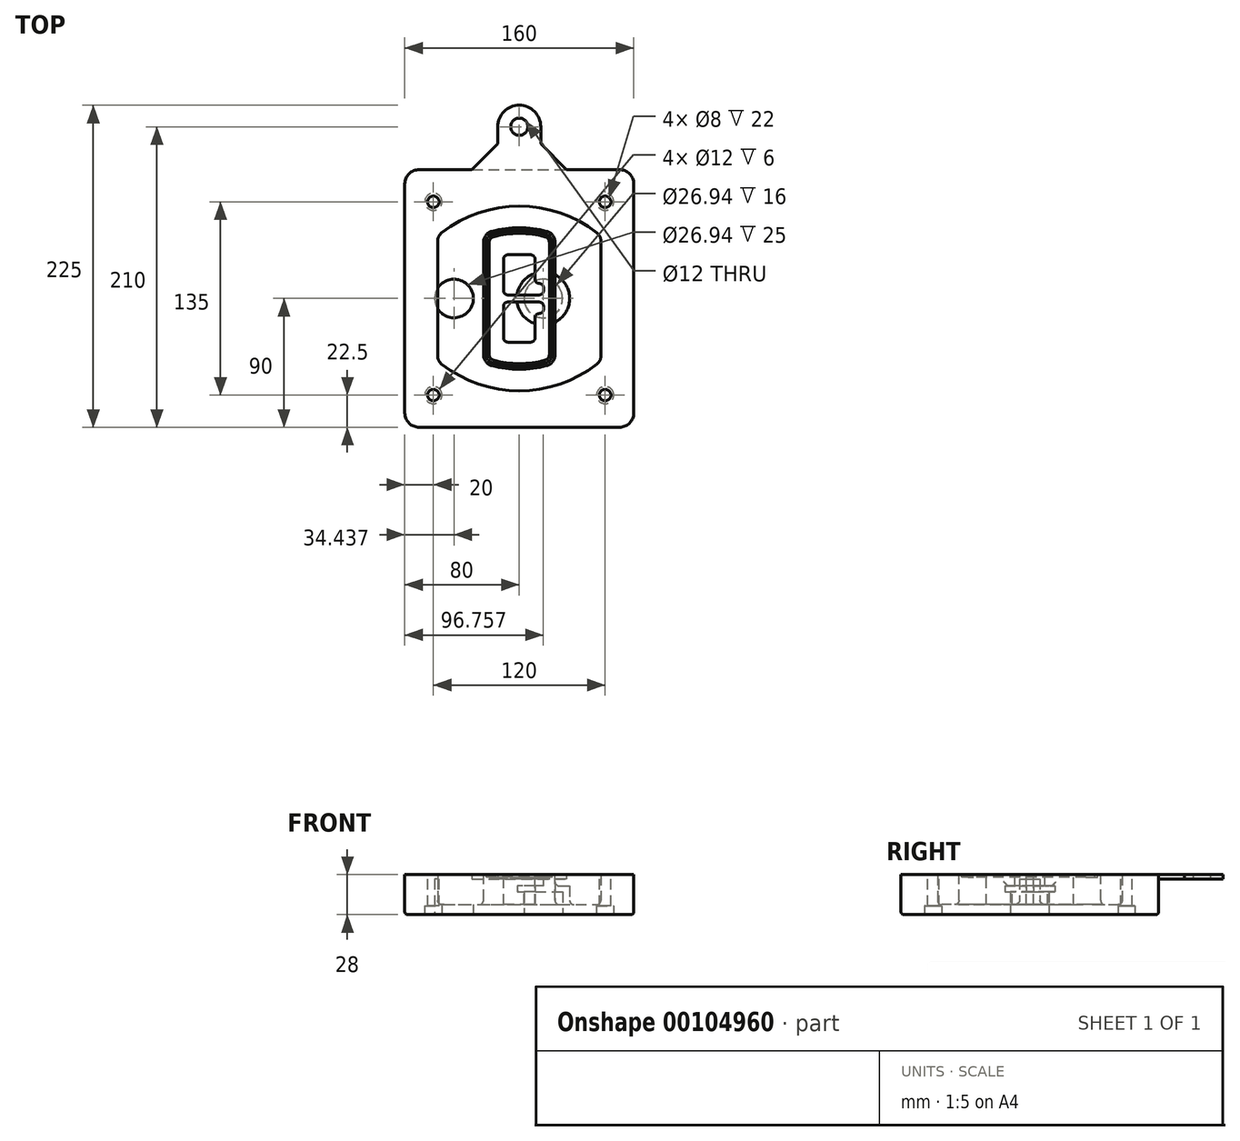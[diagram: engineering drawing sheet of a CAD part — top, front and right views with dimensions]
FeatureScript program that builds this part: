
annotation { "Feature Type Name" : "Feature", "Feature Type Description" : "" }
export const myFeature = defineFeature(function(context is Context, id is Id, definition is map)
    precondition{}
    {
        {
            var Q0;
            Q0=qCreatedBy(makeId("Top.planeOp"),FACE);
            var sketch = newSketch(context, id + "F0", { "sketchPlane" : qUnion([Q0])});
            skPoint(sketch, "E0.rect.middle", {"position": v(0, 0) * mm});
            skLineSegment(sketch, "E1.bottom", {"start": v(-70, -90) * mm, "end": v(70, -90) * mm});
            skLineSegment(sketch, "E1.top", {"start": v(-70, 90) * mm, "end": v(70, 90) * mm});
            skLineSegment(sketch, "E1.left", {"start": v(-80, -80) * mm, "end": v(-80, 80) * mm});
            skLineSegment(sketch, "E1.right", {"start": v(80, -80) * mm, "end": v(80, 80) * mm});
            skLineSegment(sketch, "E2", {"start": v(-80, 90) * mm, "end": v(80, -90) * mm, "construction": true});
            skLineSegment(sketch, "E3", {"start": v(80, 90) * mm, "end": v(-80, -90) * mm, "construction": true});
            skCircle(sketch, "E4", {"center": v(-60, 67.5) * mm, "radius": 4 * mm});
            skCircle(sketch, "E5", {"center": v(60, 67.5) * mm, "radius": 4 * mm});
            skCircle(sketch, "E6", {"center": v(60, -67.5) * mm, "radius": 4 * mm});
            skCircle(sketch, "E7", {"center": v(-60, -67.5) * mm, "radius": 4 * mm});
            skLineSegment(sketch, "E8", {"start": v(-60, 67.5) * mm, "end": v(60, 67.5) * mm, "construction": true});
            skLineSegment(sketch, "E9", {"start": v(60, 67.5) * mm, "end": v(60, -67.5) * mm, "construction": true});
            skLineSegment(sketch, "E10", {"start": v(60, -67.5) * mm, "end": v(-60, -67.5) * mm, "construction": true});
            skLineSegment(sketch, "E11", {"start": v(-60, -67.5) * mm, "end": v(-60, 67.5) * mm, "construction": true});
            skLineSegment(sketch, "E12", {"start": v(-60, 40.3) * mm, "end": v(-60, -40.3) * mm});
            skLineSegment(sketch, "E13", {"start": v(60, 40.3) * mm, "end": v(60, -40.3) * mm});
            skArc(sketch, "E14", {"start": v(56.15, 48.18) * mm, "mid": v(0, 67.5) * mm, "end": v(-56.15, 48.18) * mm});
            skArc(sketch, "E15", {"start": v(-56.15, -48.18) * mm, "mid": v(0, -67.5) * mm, "end": v(56.15, -48.18) * mm});
            skLineSegment(sketch, "E16", {"start": v(-60, 0) * mm, "end": v(60, 0) * mm, "construction": true});
            skPoint(sketch, "E17.visualSharp", {"position": v(-60, -45) * mm});
            skArc(sketch, "E17.filletArc", {"start": v(-60, -40.3) * mm, "mid": v(-58.99, -44.68) * mm, "end": v(-56.15, -48.18) * mm});
            skPoint(sketch, "E18.visualSharp", {"position": v(-60, 45) * mm});
            skArc(sketch, "E18.filletArc", {"start": v(-56.15, 48.18) * mm, "mid": v(-58.99, 44.68) * mm, "end": v(-60, 40.3) * mm});
            skPoint(sketch, "E19.visualSharp", {"position": v(60, 45) * mm});
            skArc(sketch, "E19.filletArc", {"start": v(60, 40.3) * mm, "mid": v(58.99, 44.68) * mm, "end": v(56.15, 48.18) * mm});
            skPoint(sketch, "E20.visualSharp", {"position": v(60, -45) * mm});
            skArc(sketch, "E20.filletArc", {"start": v(56.15, -48.18) * mm, "mid": v(58.99, -44.68) * mm, "end": v(60, -40.3) * mm});
            skPoint(sketch, "E21.visualSharp", {"position": v(-80, 90) * mm});
            skArc(sketch, "E21.filletArc", {"start": v(-70, 90) * mm, "mid": v(-77.07, 87.07) * mm, "end": v(-80, 80) * mm});
            skPoint(sketch, "E22.visualSharp", {"position": v(80, 90) * mm});
            skArc(sketch, "E22.filletArc", {"start": v(80, 80) * mm, "mid": v(77.07, 87.07) * mm, "end": v(70, 90) * mm});
            skPoint(sketch, "E23.visualSharp", {"position": v(80, -90) * mm});
            skArc(sketch, "E23.filletArc", {"start": v(70, -90) * mm, "mid": v(77.07, -87.07) * mm, "end": v(80, -80) * mm});
            skPoint(sketch, "E24.visualSharp", {"position": v(-80, -90) * mm});
            skArc(sketch, "E24.filletArc", {"start": v(-80, -80) * mm, "mid": v(-77.07, -87.07) * mm, "end": v(-70, -90) * mm});
            skArc(sketch, "E25.0", {"start": v(57, 40.3) * mm, "mid": v(56.3, 43.36) * mm, "end": v(54.3, 45.81) * mm});
            skLineSegment(sketch, "E25.1", {"start": v(57, 40.3) * mm, "end": v(57, -40.3) * mm});
            skArc(sketch, "E25.2", {"start": v(54.3, -45.81) * mm, "mid": v(56.3, -43.36) * mm, "end": v(57, -40.3) * mm});
            skArc(sketch, "E25.3", {"start": v(-54.3, -45.81) * mm, "mid": v(0, -64.5) * mm, "end": v(54.3, -45.81) * mm});
            skArc(sketch, "E25.4", {"start": v(-57, -40.3) * mm, "mid": v(-56.3, -43.36) * mm, "end": v(-54.3, -45.81) * mm});
            skArc(sketch, "E25.5", {"start": v(54.3, 45.81) * mm, "mid": v(0, 64.5) * mm, "end": v(-54.3, 45.81) * mm});
            skLineSegment(sketch, "E25.6", {"start": v(-57, 40.3) * mm, "end": v(-57, -40.3) * mm});
            skArc(sketch, "E25.7", {"start": v(-54.3, 45.81) * mm, "mid": v(-56.3, 43.36) * mm, "end": v(-57, 40.3) * mm});
            skArc(sketch, "E26.0", {"start": v(-58.62, 51.33) * mm, "mid": v(-62.58, 46.43) * mm, "end": v(-64, 40.3) * mm});
            skArc(sketch, "E26.1", {"start": v(58.62, 51.33) * mm, "mid": v(0, 71.5) * mm, "end": v(-58.62, 51.33) * mm});
            skArc(sketch, "E26.2", {"start": v(64, 40.3) * mm, "mid": v(62.58, 46.43) * mm, "end": v(58.62, 51.33) * mm});
            skLineSegment(sketch, "E26.3", {"start": v(64, 40.3) * mm, "end": v(64, -40.3) * mm});
            skArc(sketch, "E26.4", {"start": v(58.62, -51.33) * mm, "mid": v(62.58, -46.43) * mm, "end": v(64, -40.3) * mm});
            skLineSegment(sketch, "E26.5", {"start": v(-64, 40.3) * mm, "end": v(-64, -40.3) * mm});
            skArc(sketch, "E26.6", {"start": v(-58.62, -51.33) * mm, "mid": v(0, -71.5) * mm, "end": v(58.62, -51.33) * mm});
            skArc(sketch, "E26.7", {"start": v(-64, -40.3) * mm, "mid": v(-62.58, -46.43) * mm, "end": v(-58.62, -51.33) * mm});
            skSolve(sketch);
        }
        {
            var Q0;
            Q0=makeQuery(id+"F0.imprint","IMPRINT",FACE,{"disambiguationData":[TD([[makeQuery(id+"F0.imprint","IMPRINT",EDGE,{"derivedFrom":sQuery(id+"F0.wireOp",EDGE,"E1.bottom")}),1.0]])]});
            var Q1;
            Q1=makeQuery(id+"F0.imprint","IMPRINT",FACE,{"disambiguationData":[TD([[makeQuery(id+"F0.imprint","IMPRINT",EDGE,{"derivedFrom":sQuery(id+"F0.wireOp",EDGE,"E12")}),1.0]])]});
            var Q2;
            Q2=makeQuery(id+"F0.imprint","IMPRINT",FACE,{"disambiguationData":[TD([[makeQuery(id+"F0.imprint","IMPRINT",EDGE,{"derivedFrom":sQuery(id+"F0.wireOp",EDGE,"E25.0")}),1.0]])]});
            var Q3;
            Q3=makeQuery(id+"F0.imprint","IMPRINT",FACE,{"disambiguationData":[TD([[makeQuery(id+"F0.imprint","IMPRINT",EDGE,{"derivedFrom":sQuery(id+"F0.wireOp",EDGE,"E12")}),-1.0]])]});
            extrude(context, id + "F1", {"entities" : qUnion([Q0, Q1, Q2, Q3]), "oppositeDirection" : true, "depth" : 25 * mm});
        }
        {
            var Q0;
            Q0=makeQuery(id+"F0.imprint","IMPRINT",FACE,{"disambiguationData":[TD([[makeQuery(id+"F0.imprint","IMPRINT",EDGE,{"derivedFrom":sQuery(id+"F0.wireOp",EDGE,"E12")}),1.0]])]});
            extrude(context, id + "F2", {"entities" : qUnion([Q0]), "operationType" : NewBodyOperationType.ADD, "depth" : 3 * mm});
        }
        {
            var Q0;
            Q0=makeQuery(id+"F0.imprint","IMPRINT",FACE,{"disambiguationData":[TD([[makeQuery(id+"F0.imprint","IMPRINT",EDGE,{"derivedFrom":sQuery(id+"F0.wireOp",EDGE,"E25.0")}),1.0]])]});
            extrude(context, id + "F3", {"entities" : qUnion([Q0]), "operationType" : NewBodyOperationType.REMOVE, "oppositeDirection" : true, "depth" : 18 * mm});
        }
        {
            var Q0;
            Q0=makeQuery(id+"F2.opExtrude","CAP_FACE",FACE,{"disambiguationData":[OSD([sQuery(id+"F0.wireOp",EDGE,"E12"),sQuery(id+"F0.wireOp",EDGE,"E13"),sQuery(id+"F0.wireOp",EDGE,"E14"),sQuery(id+"F0.wireOp",EDGE,"E15"),sQuery(id+"F0.wireOp",EDGE,"E17.filletArc"),sQuery(id+"F0.wireOp",EDGE,"E18.filletArc"),sQuery(id+"F0.wireOp",EDGE,"E19.filletArc"),sQuery(id+"F0.wireOp",EDGE,"E20.filletArc"),sQuery(id+"F0.wireOp",EDGE,"E25.0"),sQuery(id+"F0.wireOp",EDGE,"E25.1"),sQuery(id+"F0.wireOp",EDGE,"E25.2"),sQuery(id+"F0.wireOp",EDGE,"E25.3"),sQuery(id+"F0.wireOp",EDGE,"E25.4"),sQuery(id+"F0.wireOp",EDGE,"E25.5"),sQuery(id+"F0.wireOp",EDGE,"E25.6"),sQuery(id+"F0.wireOp",EDGE,"E25.7")])],"isStart":false});
            var sketch = newSketch(context, id + "F4", { "sketchPlane" : qUnion([Q0])});
            skArc(sketch, "E27.0", {"start": v(-19.08, -46.97) * mm, "mid": v(0, -49.5) * mm, "end": v(19.08, -46.97) * mm});
            skArc(sketch, "E28.0", {"start": v(19.08, 46.97) * mm, "mid": v(0, 49.5) * mm, "end": v(-19.08, 46.97) * mm});
            skLineSegment(sketch, "E29", {"start": v(-25, 39.25) * mm, "end": v(-25, -39.25) * mm});
            skLineSegment(sketch, "E30", {"start": v(25, 39.25) * mm, "end": v(25, -39.25) * mm});
            skLineSegment(sketch, "E31", {"start": v(-25, 45.1) * mm, "end": v(25, 45.1) * mm, "construction": true});
            skLineSegment(sketch, "E32", {"start": v(-25, -45.1) * mm, "end": v(25, -45.1) * mm, "construction": true});
            skPoint(sketch, "E33.visualSharp", {"position": v(-25, 45.1) * mm});
            skArc(sketch, "E33.filletArc", {"start": v(-19.08, 46.97) * mm, "mid": v(-23.35, 44.11) * mm, "end": v(-25, 39.25) * mm});
            skPoint(sketch, "E34.visualSharp", {"position": v(25, 45.1) * mm});
            skArc(sketch, "E34.filletArc", {"start": v(25, 39.25) * mm, "mid": v(23.35, 44.11) * mm, "end": v(19.08, 46.97) * mm});
            skPoint(sketch, "E35.visualSharp", {"position": v(25, -45.1) * mm});
            skArc(sketch, "E35.filletArc", {"start": v(19.08, -46.97) * mm, "mid": v(23.35, -44.11) * mm, "end": v(25, -39.25) * mm});
            skPoint(sketch, "E36.visualSharp", {"position": v(-25, -45.1) * mm});
            skArc(sketch, "E36.filletArc", {"start": v(-25, -39.25) * mm, "mid": v(-23.35, -44.11) * mm, "end": v(-19.08, -46.97) * mm});
            skArc(sketch, "E37.0", {"start": v(54.3, 45.81) * mm, "mid": v(0, 64.5) * mm, "end": v(-54.3, 45.81) * mm});
            skArc(sketch, "E37.1", {"start": v(-54.3, 45.81) * mm, "mid": v(-56.3, 43.36) * mm, "end": v(-57, 40.3) * mm});
            skLineSegment(sketch, "E37.2", {"start": v(-57, 40.3) * mm, "end": v(-57, -40.3) * mm});
            skArc(sketch, "E37.3", {"start": v(-57, -40.3) * mm, "mid": v(-56.3, -43.36) * mm, "end": v(-54.3, -45.81) * mm});
            skArc(sketch, "E37.4", {"start": v(-54.3, -45.81) * mm, "mid": v(0, -64.5) * mm, "end": v(54.3, -45.81) * mm});
            skArc(sketch, "E37.5", {"start": v(54.3, -45.81) * mm, "mid": v(56.3, -43.36) * mm, "end": v(57, -40.3) * mm});
            skLineSegment(sketch, "E37.6", {"start": v(57, 40.3) * mm, "end": v(57, -40.3) * mm});
            skArc(sketch, "E37.7", {"start": v(57, 40.3) * mm, "mid": v(56.3, 43.36) * mm, "end": v(54.3, 45.81) * mm});
            skLineSegment(sketch, "E38.0", {"start": v(23, 39.25) * mm, "end": v(23, -39.25) * mm});
            skArc(sketch, "E38.1", {"start": v(18.56, -45.04) * mm, "mid": v(21.76, -42.9) * mm, "end": v(23, -39.25) * mm});
            skArc(sketch, "E38.2", {"start": v(-18.56, -45.04) * mm, "mid": v(0, -47.5) * mm, "end": v(18.56, -45.04) * mm});
            skArc(sketch, "E38.3", {"start": v(-23, -39.25) * mm, "mid": v(-21.76, -42.9) * mm, "end": v(-18.56, -45.04) * mm});
            skLineSegment(sketch, "E38.4", {"start": v(-23, 39.25) * mm, "end": v(-23, -39.25) * mm});
            skArc(sketch, "E38.5", {"start": v(23, 39.25) * mm, "mid": v(21.76, 42.9) * mm, "end": v(18.56, 45.04) * mm});
            skArc(sketch, "E38.6", {"start": v(-18.56, 45.04) * mm, "mid": v(-21.76, 42.9) * mm, "end": v(-23, 39.25) * mm});
            skArc(sketch, "E38.7", {"start": v(18.56, 45.04) * mm, "mid": v(0, 47.5) * mm, "end": v(-18.56, 45.04) * mm});
            skArc(sketch, "E39.0", {"start": v(21, 39.25) * mm, "mid": v(20.18, 41.68) * mm, "end": v(18.04, 43.1) * mm});
            skLineSegment(sketch, "E39.1", {"start": v(21, 39.25) * mm, "end": v(21, -39.25) * mm});
            skArc(sketch, "E39.2", {"start": v(18.04, -43.1) * mm, "mid": v(20.18, -41.68) * mm, "end": v(21, -39.25) * mm});
            skArc(sketch, "E39.3", {"start": v(-18.04, -43.1) * mm, "mid": v(0, -45.5) * mm, "end": v(18.04, -43.1) * mm});
            skArc(sketch, "E39.4", {"start": v(-21, -39.25) * mm, "mid": v(-20.18, -41.68) * mm, "end": v(-18.04, -43.1) * mm});
            skArc(sketch, "E39.5", {"start": v(18.04, 43.1) * mm, "mid": v(0, 45.5) * mm, "end": v(-18.04, 43.1) * mm});
            skLineSegment(sketch, "E39.6", {"start": v(-21, 39.25) * mm, "end": v(-21, -39.25) * mm});
            skArc(sketch, "E39.7", {"start": v(-18.04, 43.1) * mm, "mid": v(-20.18, 41.68) * mm, "end": v(-21, 39.25) * mm});
            skLineSegment(sketch, "E40", {"start": v(-25, 0) * mm, "end": v(25, 0) * mm, "construction": true});
            skLineSegment(sketch, "E41", {"start": v(-11, 5.5) * mm, "end": v(-11, 27.5) * mm});
            skLineSegment(sketch, "E42", {"start": v(-8, 30.5) * mm, "end": v(8, 30.5) * mm});
            skLineSegment(sketch, "E43", {"start": v(11, 27.5) * mm, "end": v(11, 13.5) * mm});
            skLineSegment(sketch, "E44", {"start": v(14, 10.5) * mm, "end": v(14, 10.5) * mm});
            skLineSegment(sketch, "E45", {"start": v(17, 7.5) * mm, "end": v(17, 5.5) * mm});
            skLineSegment(sketch, "E46", {"start": v(14, 2.5) * mm, "end": v(-8, 2.5) * mm});
            skPoint(sketch, "E47.visualSharp", {"position": v(-11, 30.5) * mm});
            skArc(sketch, "E47.filletArc", {"start": v(-8, 30.5) * mm, "mid": v(-10.12, 29.62) * mm, "end": v(-11, 27.5) * mm});
            skPoint(sketch, "E48.visualSharp", {"position": v(11, 30.5) * mm});
            skArc(sketch, "E48.filletArc", {"start": v(11, 27.5) * mm, "mid": v(10.12, 29.62) * mm, "end": v(8, 30.5) * mm});
            skPoint(sketch, "E49.visualSharp", {"position": v(11, 10.5) * mm});
            skArc(sketch, "E49.filletArc", {"start": v(11, 13.5) * mm, "mid": v(11.88, 11.38) * mm, "end": v(14, 10.5) * mm});
            skPoint(sketch, "E50.visualSharp", {"position": v(17, 10.5) * mm});
            skArc(sketch, "E50.filletArc", {"start": v(17, 7.5) * mm, "mid": v(16.12, 9.62) * mm, "end": v(14, 10.5) * mm});
            skPoint(sketch, "E51.visualSharp", {"position": v(17, 2.5) * mm});
            skArc(sketch, "E51.filletArc", {"start": v(14, 2.5) * mm, "mid": v(16.12, 3.38) * mm, "end": v(17, 5.5) * mm});
            skPoint(sketch, "E52.visualSharp", {"position": v(-11, 2.5) * mm});
            skArc(sketch, "E52.filletArc", {"start": v(-11, 5.5) * mm, "mid": v(-10.12, 3.38) * mm, "end": v(-8, 2.5) * mm});
            skLineSegment(sketch, "E53.0.MirrorCS", {"start": v(14, -2.5) * mm, "end": v(-8, -2.5) * mm});
            skArc(sketch, "E54.0.MirrorCS", {"start": v(-11, -5.5) * mm, "mid": v(-10.12, -3.38) * mm, "end": v(-8, -2.5) * mm});
            skLineSegment(sketch, "E55.0.MirrorCS", {"start": v(-11, -5.5) * mm, "end": v(-11, -27.5) * mm});
            skArc(sketch, "E56.0.MirrorCS", {"start": v(-8, -30.5) * mm, "mid": v(-10.12, -29.62) * mm, "end": v(-11, -27.5) * mm});
            skLineSegment(sketch, "E57.0.MirrorCS", {"start": v(-8, -30.5) * mm, "end": v(8, -30.5) * mm});
            skArc(sketch, "E58.0.MirrorCS", {"start": v(11, -27.5) * mm, "mid": v(10.12, -29.62) * mm, "end": v(8, -30.5) * mm});
            skLineSegment(sketch, "E59.0.MirrorCS", {"start": v(11, -27.5) * mm, "end": v(11, -13.5) * mm});
            skArc(sketch, "E60.0.MirrorCS", {"start": v(11, -13.5) * mm, "mid": v(11.88, -11.38) * mm, "end": v(14, -10.5) * mm});
            skArc(sketch, "E61.0.MirrorCS", {"start": v(17, -7.5) * mm, "mid": v(16.12, -9.62) * mm, "end": v(14, -10.5) * mm});
            skLineSegment(sketch, "E62.0.MirrorCS", {"start": v(17, -7.5) * mm, "end": v(17, -5.5) * mm});
            skArc(sketch, "E63.0.MirrorCS", {"start": v(14, -2.5) * mm, "mid": v(16.12, -3.38) * mm, "end": v(17, -5.5) * mm});
            skSolve(sketch);
        }
        {
            var Q0;
            Q0=makeQuery(id+"F4.imprint","IMPRINT",FACE,{"disambiguationData":[TD([[makeQuery(id+"F4.imprint","IMPRINT",EDGE,{"derivedFrom":sQuery(id+"F4.wireOp",EDGE,"E27.0")}),1.0]])]});
            var Q1;
            Q1=makeQuery(id+"F4.imprint","IMPRINT",FACE,{"disambiguationData":[TD([[makeQuery(id+"F4.imprint","IMPRINT",EDGE,{"derivedFrom":sQuery(id+"F4.wireOp",EDGE,"E38.0")}),-1.0]])]});
            var Q2;
            Q2=makeQuery(id+"F4.imprint","IMPRINT",FACE,{"disambiguationData":[TD([[makeQuery(id+"F4.imprint","IMPRINT",EDGE,{"derivedFrom":sQuery(id+"F4.wireOp",EDGE,"E39.0")}),1.0]])]});
            extrude(context, id + "F5", {"entities" : qUnion([Q0, Q1, Q2]), "operationType" : NewBodyOperationType.ADD, "endBound" : BoundingType.UP_TO_NEXT, "oppositeDirection" : true, "depth" : 25 * mm});
        }
        {
            var Q0;
            Q0=makeQuery(id+"F4.imprint","IMPRINT",FACE,{"disambiguationData":[TD([[makeQuery(id+"F4.imprint","IMPRINT",EDGE,{"derivedFrom":sQuery(id+"F4.wireOp",EDGE,"E38.0")}),-1.0]])]});
            extrude(context, id + "F6", {"entities" : qUnion([Q0]), "operationType" : NewBodyOperationType.REMOVE, "oppositeDirection" : true, "depth" : 2 * mm});
        }
        {
            var Q0;
            Q0=makeQuery(id+"F1.opExtrude","CAP_FACE",FACE,{"disambiguationData":[OSD([sQuery(id+"F0.wireOp",EDGE,"E1.bottom"),sQuery(id+"F0.wireOp",EDGE,"E1.top"),sQuery(id+"F0.wireOp",EDGE,"E1.left"),sQuery(id+"F0.wireOp",EDGE,"E1.right"),sQuery(id+"F0.wireOp",EDGE,"E4"),sQuery(id+"F0.wireOp",EDGE,"E5"),sQuery(id+"F0.wireOp",EDGE,"E6"),sQuery(id+"F0.wireOp",EDGE,"E7"),sQuery(id+"F0.wireOp",EDGE,"E21.filletArc"),sQuery(id+"F0.wireOp",EDGE,"E22.filletArc"),sQuery(id+"F0.wireOp",EDGE,"E23.filletArc"),sQuery(id+"F0.wireOp",EDGE,"E24.filletArc")])],"isStart":false});
            var sketch = newSketch(context, id + "F7", { "sketchPlane" : qUnion([Q0])});
            skCircle(sketch, "E64", {"center": v(16.76, 0) * mm, "radius": 13.47 * mm});
            skCircle(sketch, "E65", {"center": v(-45.56, 0) * mm, "radius": 13.47 * mm});
            skLineSegment(sketch, "E66", {"start": v(80, 0) * mm, "end": v(-80, 0) * mm});
            skCircle(sketch, "E67", {"center": v(16.76, 0) * mm, "radius": 18.47 * mm});
            skCircle(sketch, "E68", {"center": v(60, -67.5) * mm, "radius": 6 * mm});
            skCircle(sketch, "E69", {"center": v(-60, -67.5) * mm, "radius": 6 * mm});
            skCircle(sketch, "E70", {"center": v(-60, 67.5) * mm, "radius": 6 * mm});
            skCircle(sketch, "E71", {"center": v(60, 67.5) * mm, "radius": 6 * mm});
            skSolve(sketch);
        }
        {
            var Q0;
            {var subQ1=sQuery(id+"F7.wireOp",EDGE,"E66");var subQ4=sQuery(id+"F7.wireOp",EDGE,"E64");var subQ6=makeQuery(id+"F7.imprint","INTERSECT",VERTEX,{"disambiguationData":[OD(0.0)],"derivedFrom":[subQ4,subQ1]});Q0=makeQuery(id+"F7.imprint","IMPRINT",FACE,{"disambiguationData":[TD([[makeQuery(id+"F7.imprint","IMPRINT",EDGE,{"disambiguationData":[TD([[subQ6,-1.0]])],"derivedFrom":subQ4}),-1.0]])]});}
            var Q1;
            {var subQ0=sQuery(id+"F7.wireOp",EDGE,"E66");var subQ1=sQuery(id+"F7.wireOp",EDGE,"E64");var subQ3=makeQuery(id+"F7.imprint","INTERSECT",VERTEX,{"disambiguationData":[OD(0.0)],"derivedFrom":[subQ1,subQ0]});Q1=makeQuery(id+"F7.imprint","IMPRINT",FACE,{"disambiguationData":[TD([[makeQuery(id+"F7.imprint","IMPRINT",EDGE,{"disambiguationData":[TD([[subQ3,-1.0]])],"derivedFrom":subQ1}),1.0]])]});}
            var Q2;
            {var subQ0=sQuery(id+"F7.wireOp",EDGE,"E66");var subQ1=sQuery(id+"F7.wireOp",EDGE,"E64");var subQ3=makeQuery(id+"F7.imprint","INTERSECT",VERTEX,{"disambiguationData":[OD(0.0)],"derivedFrom":[subQ1,subQ0]});Q2=makeQuery(id+"F7.imprint","IMPRINT",FACE,{"disambiguationData":[TD([[makeQuery(id+"F7.imprint","IMPRINT",EDGE,{"disambiguationData":[TD([[subQ3,1.0]])],"derivedFrom":subQ1}),1.0]])]});}
            var Q3;
            {var subQ1=sQuery(id+"F7.wireOp",EDGE,"E66");var subQ4=sQuery(id+"F7.wireOp",EDGE,"E64");var subQ6=makeQuery(id+"F7.imprint","INTERSECT",VERTEX,{"disambiguationData":[OD(0.0)],"derivedFrom":[subQ4,subQ1]});Q3=makeQuery(id+"F7.imprint","IMPRINT",FACE,{"disambiguationData":[TD([[makeQuery(id+"F7.imprint","IMPRINT",EDGE,{"disambiguationData":[TD([[subQ6,1.0]])],"derivedFrom":subQ4}),-1.0]])]});}
            extrude(context, id + "F8", {"entities" : qUnion([Q0, Q1, Q2, Q3]), "operationType" : NewBodyOperationType.ADD, "oppositeDirection" : true, "depth" : 20 * mm});
        }
        {
            var Q0;
            {var subQ0=sQuery(id+"F7.wireOp",EDGE,"E66");var subQ1=sQuery(id+"F7.wireOp",EDGE,"E64");var subQ3=makeQuery(id+"F7.imprint","INTERSECT",VERTEX,{"disambiguationData":[OD(0.0)],"derivedFrom":[subQ1,subQ0]});Q0=makeQuery(id+"F7.imprint","IMPRINT",FACE,{"disambiguationData":[TD([[makeQuery(id+"F7.imprint","IMPRINT",EDGE,{"disambiguationData":[TD([[subQ3,-1.0]])],"derivedFrom":subQ1}),1.0]])]});}
            var Q1;
            {var subQ0=sQuery(id+"F7.wireOp",EDGE,"E66");var subQ1=sQuery(id+"F7.wireOp",EDGE,"E64");var subQ3=makeQuery(id+"F7.imprint","INTERSECT",VERTEX,{"disambiguationData":[OD(0.0)],"derivedFrom":[subQ1,subQ0]});Q1=makeQuery(id+"F7.imprint","IMPRINT",FACE,{"disambiguationData":[TD([[makeQuery(id+"F7.imprint","IMPRINT",EDGE,{"disambiguationData":[TD([[subQ3,1.0]])],"derivedFrom":subQ1}),1.0]])]});}
            extrude(context, id + "F9", {"entities" : qUnion([Q0, Q1]), "operationType" : NewBodyOperationType.REMOVE, "oppositeDirection" : true, "depth" : 16 * mm});
        }
        {
            var Q0;
            {var subQ0=sQuery(id+"F7.wireOp",EDGE,"E66");var subQ1=sQuery(id+"F7.wireOp",EDGE,"E65");var subQ3=makeQuery(id+"F7.imprint","INTERSECT",VERTEX,{"disambiguationData":[OD(0.0)],"derivedFrom":[subQ1,subQ0]});Q0=makeQuery(id+"F7.imprint","IMPRINT",FACE,{"disambiguationData":[TD([[makeQuery(id+"F7.imprint","IMPRINT",EDGE,{"disambiguationData":[TD([[subQ3,-1.0]])],"derivedFrom":subQ1}),1.0]])]});}
            var Q1;
            {var subQ0=sQuery(id+"F7.wireOp",EDGE,"E66");var subQ1=sQuery(id+"F7.wireOp",EDGE,"E65");var subQ3=makeQuery(id+"F7.imprint","INTERSECT",VERTEX,{"disambiguationData":[OD(0.0)],"derivedFrom":[subQ1,subQ0]});Q1=makeQuery(id+"F7.imprint","IMPRINT",FACE,{"disambiguationData":[TD([[makeQuery(id+"F7.imprint","IMPRINT",EDGE,{"disambiguationData":[TD([[subQ3,1.0]])],"derivedFrom":subQ1}),1.0]])]});}
            extrude(context, id + "F10", {"entities" : qUnion([Q0, Q1]), "operationType" : NewBodyOperationType.REMOVE, "oppositeDirection" : true, "depth" : 25 * mm});
        }
        {
            var Q0;
            Q0=makeQuery(id+"F7.imprint","IMPRINT",FACE,{"disambiguationData":[TD([[makeQuery(id+"F7.imprint","IMPRINT",EDGE,{"derivedFrom":sQuery(id+"F7.wireOp",EDGE,"E68")}),1.0]])]});
            var Q1;
            Q1=makeQuery(id+"F7.imprint","IMPRINT",FACE,{"disambiguationData":[TD([[makeQuery(id+"F7.imprint","IMPRINT",EDGE,{"derivedFrom":makeQuery(id+"F1.opExtrude","CAP_EDGE",EDGE,{"disambiguationData":[OSD([sQuery(id+"F0.wireOp",EDGE,"E5")])],"isStart":false})}),-1.0]])]});
            var Q2;
            Q2=makeQuery(id+"F7.imprint","IMPRINT",FACE,{"disambiguationData":[TD([[makeQuery(id+"F7.imprint","IMPRINT",EDGE,{"derivedFrom":sQuery(id+"F7.wireOp",EDGE,"E69")}),1.0]])]});
            var Q3;
            Q3=makeQuery(id+"F7.imprint","IMPRINT",FACE,{"disambiguationData":[TD([[makeQuery(id+"F7.imprint","IMPRINT",EDGE,{"derivedFrom":makeQuery(id+"F1.opExtrude","CAP_EDGE",EDGE,{"disambiguationData":[OSD([sQuery(id+"F0.wireOp",EDGE,"E4")])],"isStart":false})}),-1.0]])]});
            var Q4;
            Q4=makeQuery(id+"F7.imprint","IMPRINT",FACE,{"disambiguationData":[TD([[makeQuery(id+"F7.imprint","IMPRINT",EDGE,{"derivedFrom":sQuery(id+"F7.wireOp",EDGE,"E70")}),1.0]])]});
            var Q5;
            Q5=makeQuery(id+"F7.imprint","IMPRINT",FACE,{"disambiguationData":[TD([[makeQuery(id+"F7.imprint","IMPRINT",EDGE,{"derivedFrom":makeQuery(id+"F1.opExtrude","CAP_EDGE",EDGE,{"disambiguationData":[OSD([sQuery(id+"F0.wireOp",EDGE,"E7")])],"isStart":false})}),-1.0]])]});
            var Q6;
            Q6=makeQuery(id+"F7.imprint","IMPRINT",FACE,{"disambiguationData":[TD([[makeQuery(id+"F7.imprint","IMPRINT",EDGE,{"derivedFrom":sQuery(id+"F7.wireOp",EDGE,"E71")}),1.0]])]});
            var Q7;
            Q7=makeQuery(id+"F7.imprint","IMPRINT",FACE,{"disambiguationData":[TD([[makeQuery(id+"F7.imprint","IMPRINT",EDGE,{"derivedFrom":makeQuery(id+"F1.opExtrude","CAP_EDGE",EDGE,{"disambiguationData":[OSD([sQuery(id+"F0.wireOp",EDGE,"E6")])],"isStart":false})}),-1.0]])]});
            extrude(context, id + "F11", {"entities" : qUnion([Q0, Q1, Q2, Q3, Q4, Q5, Q6, Q7]), "operationType" : NewBodyOperationType.REMOVE, "oppositeDirection" : true, "depth" : 6 * mm});
        }
        {
            var Q0;
            Q0=makeQuery(id+"F9.boolean.opBoolean","COPY",FACE,{"derivedFrom":makeQuery(id+"F9.opExtrude","CAP_FACE",FACE,{"disambiguationData":[OSD([sQuery(id+"F7.wireOp",EDGE,"E64")])],"isStart":false})});
            var sketch = newSketch(context, id + "F12", { "sketchPlane" : qUnion([Q0])});
            skArc(sketch, "E72.0", {"start": v(11, 17.55) * mm, "mid": v(2.57, 11.82) * mm, "end": v(-1.54, 2.5) * mm});
            skArc(sketch, "E72.1", {"start": v(-1.54, -2.5) * mm, "mid": v(2.57, -11.82) * mm, "end": v(11, -17.55) * mm});
            skLineSegment(sketch, "E73", {"start": v(-1.54, -2.5) * mm, "end": v(14, -2.5) * mm});
            skLineSegment(sketch, "E74.0", {"start": v(14, 2.5) * mm, "end": v(-1.54, 2.5) * mm});
            skArc(sketch, "E74.1", {"start": v(14, 2.5) * mm, "mid": v(16.12, 3.38) * mm, "end": v(17, 5.5) * mm});
            skLineSegment(sketch, "E74.2", {"start": v(17, 7.5) * mm, "end": v(17, 5.5) * mm});
            skArc(sketch, "E74.3", {"start": v(17, 7.5) * mm, "mid": v(16.12, 9.62) * mm, "end": v(14, 10.5) * mm});
            skArc(sketch, "E74.4", {"start": v(11, 13.5) * mm, "mid": v(11.88, 11.38) * mm, "end": v(14, 10.5) * mm});
            skLineSegment(sketch, "E74.5", {"start": v(11, 17.55) * mm, "end": v(11, 13.5) * mm});
            skLineSegment(sketch, "E74.7", {"start": v(14, -2.5) * mm, "end": v(-1.54, -2.5) * mm});
            skArc(sketch, "E74.8", {"start": v(14, -2.5) * mm, "mid": v(16.12, -3.38) * mm, "end": v(17, -5.5) * mm});
            skLineSegment(sketch, "E74.9", {"start": v(17, -7.5) * mm, "end": v(17, -5.5) * mm});
            skArc(sketch, "E74.10", {"start": v(17, -7.5) * mm, "mid": v(16.12, -9.62) * mm, "end": v(14, -10.5) * mm});
            skArc(sketch, "E74.11", {"start": v(11, -13.5) * mm, "mid": v(11.88, -11.38) * mm, "end": v(14, -10.5) * mm});
            skLineSegment(sketch, "E74.12", {"start": v(11, -17.55) * mm, "end": v(11, -13.5) * mm});
            skPoint(sketch, "E75.orphan", {"position": v(11, -27.5) * mm});
            skPoint(sketch, "E76.orphan", {"position": v(-8, -2.5) * mm});
            skPoint(sketch, "E77.orphan", {"position": v(-8, 2.5) * mm});
            skPoint(sketch, "E78.orphan", {"position": v(11, 27.5) * mm});
            skSolve(sketch);
        }
        {
            var Q0;
            {var subQ7=sQuery(id+"F12.wireOp",EDGE,"E72.0");var subQ14=sQuery(id+"F12.wireOp",EDGE,"E72.1");var subQ16=sQuery(id+"F12.wireOp",EDGE,"E74.1");var subQ18=sQuery(id+"F12.wireOp",EDGE,"E74.8");Q0=qUnion([makeQuery(id+"F12.imprint","IMPRINT",FACE,{"disambiguationData":[TD([[makeQuery(id+"F12.imprint","IMPRINT",EDGE,{"derivedFrom":subQ7}),1.0]])]}),makeQuery(id+"F12.imprint","IMPRINT",FACE,{"disambiguationData":[TD([[makeQuery(id+"F12.imprint","IMPRINT",EDGE,{"derivedFrom":subQ14}),1.0]])]}),makeQuery(id+"F12.imprint","IMPRINT",FACE,{"disambiguationData":[TD([[makeQuery(id+"F12.imprint","IMPRINT",EDGE,{"derivedFrom":subQ16}),1.0]])]}),makeQuery(id+"F12.imprint","IMPRINT",FACE,{"disambiguationData":[TD([[makeQuery(id+"F12.imprint","IMPRINT",EDGE,{"derivedFrom":subQ18}),-1.0]])]})]);}
            var Q1;
            Q1=makeQuery(id+"F5.boolean.opBoolean","SPLIT",FACE,{"disambiguationData":[TD([makeQuery(id+"F5.opExtrude","SWEPT_FACE",FACE,{"disambiguationData":[OSD([sQuery(id+"F4.wireOp",EDGE,"E41")])]})])],"derivedFrom":makeQuery(id+"F3.boolean.opBoolean","COPY",FACE,{"derivedFrom":makeQuery(id+"F3.opExtrude","CAP_FACE",FACE,{"disambiguationData":[OSD([sQuery(id+"F0.wireOp",EDGE,"E25.0"),sQuery(id+"F0.wireOp",EDGE,"E25.1"),sQuery(id+"F0.wireOp",EDGE,"E25.2"),sQuery(id+"F0.wireOp",EDGE,"E25.3"),sQuery(id+"F0.wireOp",EDGE,"E25.4"),sQuery(id+"F0.wireOp",EDGE,"E25.5"),sQuery(id+"F0.wireOp",EDGE,"E25.6"),sQuery(id+"F0.wireOp",EDGE,"E25.7")])],"isStart":false})})});
            extrude(context, id + "F13", {"entities" : qUnion([Q0]), "operationType" : NewBodyOperationType.REMOVE, "endBound" : BoundingType.UP_TO_SURFACE, "endBoundEntityFace" : qUnion([Q1]), "depth" : 25 * mm});
        }
        {
            var Q0;
            Q0=makeQuery(id+"F3.boolean.opBoolean","COPY",EDGE,{"derivedFrom":makeQuery(id+"F3.opExtrude","CAP_EDGE",EDGE,{"disambiguationData":[OSD([sQuery(id+"F0.wireOp",EDGE,"E25.6")])],"isStart":false})});
            var Q1;
            Q1=makeQuery(id+"F8.boolean.opBoolean","INTERSECT",EDGE,{"derivedFrom":[makeQuery(id+"F5.opExtrude","SWEPT_FACE",FACE,{"disambiguationData":[OSD([sQuery(id+"F4.wireOp",EDGE,"E30")])]}),makeQuery(id+"F8.opExtrude","CAP_FACE",FACE,{"disambiguationData":[OSD([sQuery(id+"F7.wireOp",EDGE,"E67")])],"isStart":false})]});
            var Q2;
            Q2=makeQuery(id+"F8.boolean.opBoolean","INTERSECT",EDGE,{"disambiguationData":[OD(1.0)],"derivedFrom":[makeQuery(id+"F5.opExtrude","SWEPT_FACE",FACE,{"disambiguationData":[OSD([sQuery(id+"F4.wireOp",EDGE,"E30")])]}),makeQuery(id+"F8.opExtrude","SWEPT_FACE",FACE,{"disambiguationData":[OSD([sQuery(id+"F7.wireOp",EDGE,"E67")])]})]});
            var Q3;
            {var subQ0=sQuery(id+"F4.wireOp",EDGE,"E30");Q3=makeQuery(id+"F8.boolean.opBoolean","SPLIT",EDGE,{"disambiguationData":[TD([makeQuery(id+"F5.opExtrude","SWEPT_FACE",FACE,{"disambiguationData":[OSD([sQuery(id+"F4.wireOp",EDGE,"E35.filletArc")])]})])],"derivedFrom":makeQuery(id+"F5.opExtrude","CAP_EDGE",EDGE,{"disambiguationData":[OSD([subQ0])],"isStart":false})});}
            var Q4;
            {var subQ0=sQuery(id+"F0.wireOp",EDGE,"E25.7");var subQ1=sQuery(id+"F0.wireOp",EDGE,"E25.1");var subQ2=sQuery(id+"F0.wireOp",EDGE,"E25.6");var subQ3=sQuery(id+"F0.wireOp",EDGE,"E25.5");var subQ4=sQuery(id+"F0.wireOp",EDGE,"E25.4");var subQ5=sQuery(id+"F0.wireOp",EDGE,"E25.0");var subQ6=sQuery(id+"F0.wireOp",EDGE,"E25.2");var subQ7=sQuery(id+"F0.wireOp",EDGE,"E25.3");Q4=makeQuery(id+"F8.boolean.opBoolean","INTERSECT",EDGE,{"derivedFrom":[makeQuery(id+"F5.boolean.opBoolean","SPLIT",FACE,{"disambiguationData":[TD([makeQuery(id+"F2.opExtrude","SWEPT_FACE",FACE,{"disambiguationData":[OSD([subQ5])]})])],"derivedFrom":makeQuery(id+"F3.boolean.opBoolean","COPY",FACE,{"derivedFrom":makeQuery(id+"F3.opExtrude","CAP_FACE",FACE,{"disambiguationData":[OSD([subQ5,subQ1,subQ6,subQ7,subQ4,subQ3,subQ2,subQ0])],"isStart":false})})}),makeQuery(id+"F8.opExtrude","SWEPT_FACE",FACE,{"disambiguationData":[OSD([sQuery(id+"F7.wireOp",EDGE,"E67")])]})]});}
            var Q5;
            Q5=makeQuery(id+"F8.boolean.opBoolean","INTERSECT",EDGE,{"disambiguationData":[OD(0.0)],"derivedFrom":[makeQuery(id+"F5.opExtrude","SWEPT_FACE",FACE,{"disambiguationData":[OSD([sQuery(id+"F4.wireOp",EDGE,"E30")])]}),makeQuery(id+"F8.opExtrude","SWEPT_FACE",FACE,{"disambiguationData":[OSD([sQuery(id+"F7.wireOp",EDGE,"E67")])]})]});
            fillet(context, id + "F14", {"entities" : qUnion([Q0, Q1, Q2, Q3, Q4, Q5]), "radius" : 3 * mm, "tangentPropagation" : true, "allowEdgeOverflow" : false});
        }
        {
            var Q0;
            Q0=makeQuery(id+"F1.opExtrude","CAP_EDGE",EDGE,{"disambiguationData":[OSD([sQuery(id+"F0.wireOp",EDGE,"E1.bottom")])],"isStart":false});
            fillet(context, id + "F15", {"entities" : qUnion([Q0]), "radius" : 2 * mm, "tangentPropagation" : true, "allowEdgeOverflow" : false});
        }
        {
            var Q0;
            {var subQ0=sQuery(id+"F0.wireOp",EDGE,"E22.filletArc");var subQ1=sQuery(id+"F0.wireOp",EDGE,"E7");var subQ2=sQuery(id+"F0.wireOp",EDGE,"E6");var subQ3=sQuery(id+"F0.wireOp",EDGE,"E5");var subQ4=sQuery(id+"F0.wireOp",EDGE,"E4");var subQ5=sQuery(id+"F0.wireOp",EDGE,"E1.bottom");var subQ6=sQuery(id+"F0.wireOp",EDGE,"E21.filletArc");var subQ7=sQuery(id+"F0.wireOp",EDGE,"E1.top");var subQ8=sQuery(id+"F0.wireOp",EDGE,"E1.left");var subQ9=sQuery(id+"F0.wireOp",EDGE,"E1.right");var subQ10=sQuery(id+"F0.wireOp",EDGE,"E23.filletArc");var subQ11=sQuery(id+"F0.wireOp",EDGE,"E24.filletArc");Q0=makeQuery(id+"F2.boolean.opBoolean","SPLIT",FACE,{"disambiguationData":[TD([makeQuery(id+"F1.opExtrude","SWEPT_FACE",FACE,{"disambiguationData":[OSD([subQ5])]})])],"derivedFrom":makeQuery(id+"F1.opExtrude","CAP_FACE",FACE,{"disambiguationData":[OSD([subQ5,subQ7,subQ8,subQ9,subQ4,subQ3,subQ2,subQ1,subQ6,subQ0,subQ10,subQ11])],"isStart":true})});}
            var sketch = newSketch(context, id + "F16", { "sketchPlane" : qUnion([Q0])});
            skLineSegment(sketch, "E79", {"start": v(0, 90) * mm, "end": v(0, 120) * mm, "construction": true});
            skCircle(sketch, "E80", {"center": v(0, 120) * mm, "radius": 6 * mm});
            skLineSegment(sketch, "E81", {"start": v(-33, 90) * mm, "end": v(-15, 108) * mm});
            skLineSegment(sketch, "E82", {"start": v(33, 90) * mm, "end": v(15, 108) * mm});
            skLineSegment(sketch, "E83", {"start": v(-15, 108) * mm, "end": v(-15, 120) * mm});
            skLineSegment(sketch, "E84", {"start": v(15, 108) * mm, "end": v(15, 120) * mm});
            skArc(sketch, "E85", {"start": v(15, 120) * mm, "mid": v(0, 135) * mm, "end": v(-15, 120) * mm});
            skLineSegment(sketch, "E86", {"start": v(-80, 0) * mm, "end": v(80, 0) * mm, "construction": true});
            skArc(sketch, "E87.MirrorCS", {"start": v(15, -120) * mm, "mid": v(0, -135) * mm, "end": v(-15, -120) * mm});
            skLineSegment(sketch, "E88.MirrorCS", {"start": v(15, -108) * mm, "end": v(15, -120) * mm});
            skCircle(sketch, "E89.MirrorC", {"center": v(0, -120) * mm, "radius": 6 * mm});
            skLineSegment(sketch, "E90.MirrorCS", {"start": v(-15, -108) * mm, "end": v(-15, -120) * mm});
            skLineSegment(sketch, "E91.MirrorCS", {"start": v(-33, -90) * mm, "end": v(-15, -108) * mm});
            skLineSegment(sketch, "E92.MirrorCS", {"start": v(33, -90) * mm, "end": v(15, -108) * mm});
            skSolve(sketch);
        }
        {
            var Q0;
            Q0=makeQuery(id+"F16.imprint","IMPRINT",FACE,{"disambiguationData":[TD([[makeQuery(id+"F16.imprint","IMPRINT",EDGE,{"derivedFrom":sQuery(id+"F16.wireOp",EDGE,"E87.MirrorCS")}),-1.0]])]});
            var Q1;
            Q1=makeQuery(id+"F16.imprint","IMPRINT",FACE,{"disambiguationData":[TD([[makeQuery(id+"F16.imprint","IMPRINT",EDGE,{"derivedFrom":makeQuery(id+"F1.opExtrude","CAP_EDGE",EDGE,{"disambiguationData":[OSD([sQuery(id+"F0.wireOp",EDGE,"E1.left")])],"isStart":true})}),-1.0]])]});
            var Q2;
            Q2=makeQuery(id+"F16.imprint","IMPRINT",FACE,{"disambiguationData":[TD([[makeQuery(id+"F16.imprint","IMPRINT",EDGE,{"derivedFrom":sQuery(id+"F16.wireOp",EDGE,"E80")}),-1.0]])]});
            var Q3;
            Q3=makeQuery(id+"F2.opExtrude","CAP_FACE",FACE,{"disambiguationData":[OSD([sQuery(id+"F0.wireOp",EDGE,"E12"),sQuery(id+"F0.wireOp",EDGE,"E13"),sQuery(id+"F0.wireOp",EDGE,"E14"),sQuery(id+"F0.wireOp",EDGE,"E15"),sQuery(id+"F0.wireOp",EDGE,"E17.filletArc"),sQuery(id+"F0.wireOp",EDGE,"E18.filletArc"),sQuery(id+"F0.wireOp",EDGE,"E19.filletArc"),sQuery(id+"F0.wireOp",EDGE,"E20.filletArc"),sQuery(id+"F0.wireOp",EDGE,"E25.0"),sQuery(id+"F0.wireOp",EDGE,"E25.1"),sQuery(id+"F0.wireOp",EDGE,"E25.2"),sQuery(id+"F0.wireOp",EDGE,"E25.3"),sQuery(id+"F0.wireOp",EDGE,"E25.4"),sQuery(id+"F0.wireOp",EDGE,"E25.5"),sQuery(id+"F0.wireOp",EDGE,"E25.6"),sQuery(id+"F0.wireOp",EDGE,"E25.7")])],"isStart":false});
            extrude(context, id + "F17", {"entities" : qUnion([Q0, Q1, Q2]), "operationType" : NewBodyOperationType.ADD, "endBound" : BoundingType.UP_TO_SURFACE, "endBoundEntityFace" : qUnion([Q3]), "depth" : 25 * mm});
        }
    });
